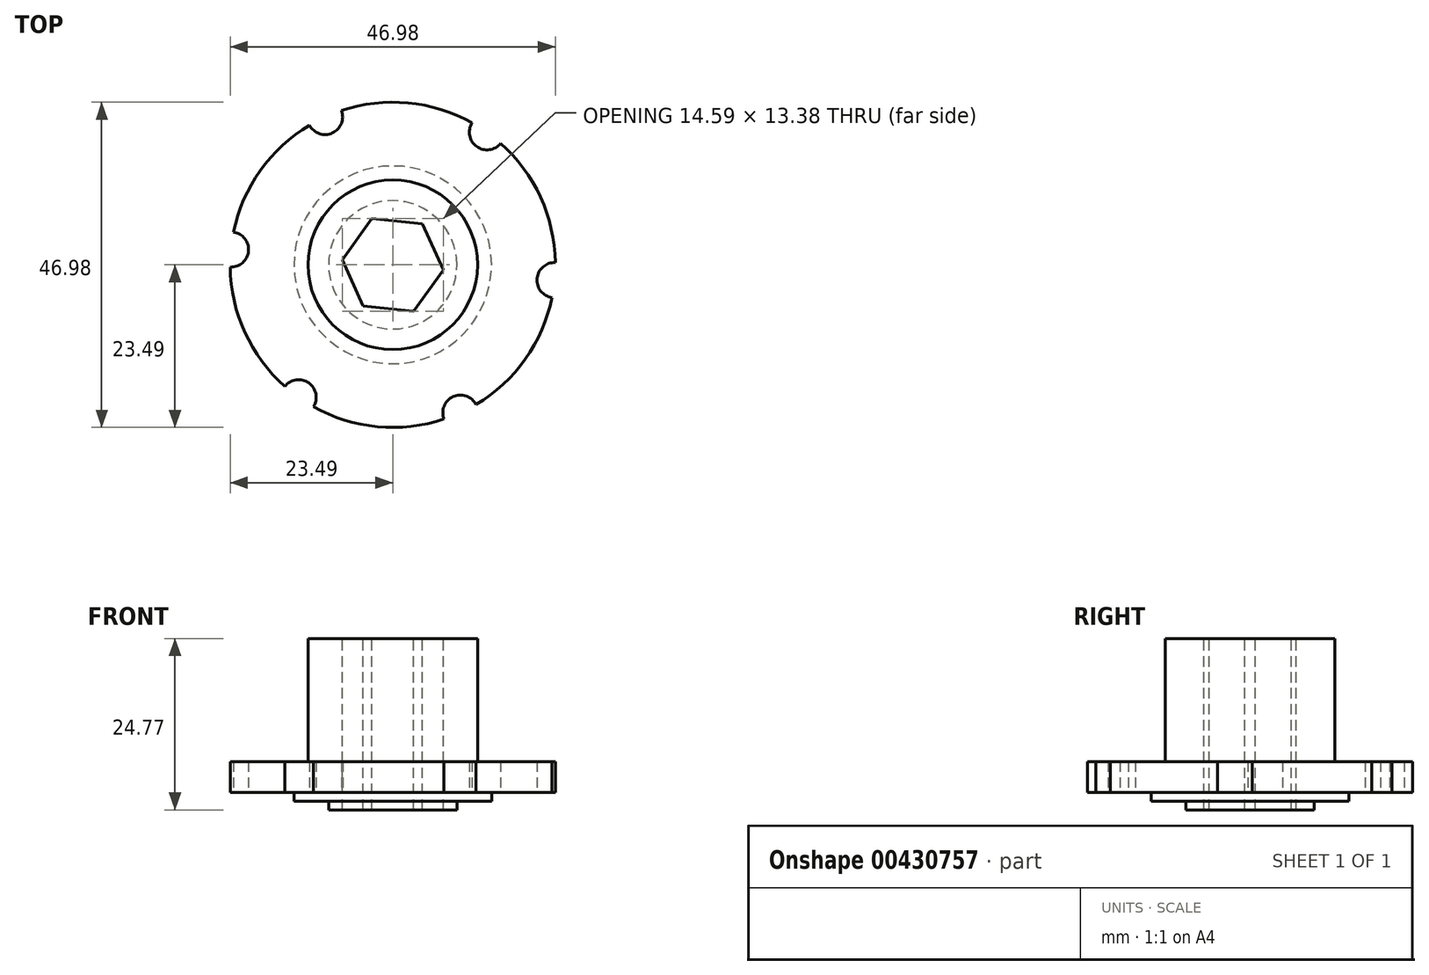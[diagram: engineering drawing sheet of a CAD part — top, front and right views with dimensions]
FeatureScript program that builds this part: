
annotation { "Feature Type Name" : "Feature", "Feature Type Description" : "" }
export const myFeature = defineFeature(function(context is Context, id is Id, definition is map)
    precondition{}
    {
        {
            var Q0;
            Q0=qCreatedBy(makeId("Top.planeOp"),FACE);
            var sketch = newSketch(context, id + "F0", { "sketchPlane" : qUnion([Q0])});
            skCircle(sketch, "E0", {"center": v(0, 0) * mm, "radius": 27.3 * mm});
            skCircle(sketch, "E1", {"center": v(0, 0) * mm, "radius": 23.5 * mm});
            skCircle(sketch, "E2", {"center": v(0, 0) * mm, "radius": 14.29 * mm});
            skCircle(sketch, "E3", {"center": v(0, 0) * mm, "radius": 9.27 * mm});
            skCircle(sketch, "E4.cCircle", {"center": v(0, 0) * mm, "radius": 23.5 * mm, "construction": true});
            skLineSegment(sketch, "E4.0", {"start": v(-9.78, 21.36) * mm, "end": v(13.6, 19.15) * mm});
            skLineSegment(sketch, "E4.1", {"start": v(13.6, 19.15) * mm, "end": v(23.4, -2.2) * mm});
            skLineSegment(sketch, "E4.2", {"start": v(23.4, -2.2) * mm, "end": v(9.78, -21.36) * mm});
            skLineSegment(sketch, "E4.3", {"start": v(9.78, -21.36) * mm, "end": v(-13.6, -19.15) * mm});
            skLineSegment(sketch, "E4.4", {"start": v(-13.6, -19.15) * mm, "end": v(-23.4, 2.2) * mm});
            skLineSegment(sketch, "E4.5", {"start": v(-23.4, 2.2) * mm, "end": v(-9.78, 21.36) * mm});
            skCircle(sketch, "E5", {"center": v(9.78, -21.36) * mm, "radius": 2.54 * mm});
            skCircle(sketch, "E6", {"center": v(-13.6, -19.15) * mm, "radius": 2.54 * mm});
            skCircle(sketch, "E7", {"center": v(23.4, -2.2) * mm, "radius": 2.54 * mm});
            skCircle(sketch, "E8", {"center": v(13.6, 19.15) * mm, "radius": 2.54 * mm});
            skCircle(sketch, "E9", {"center": v(-9.78, 21.36) * mm, "radius": 2.54 * mm});
            skCircle(sketch, "E10", {"center": v(-23.4, 2.2) * mm, "radius": 2.54 * mm});
            skSolve(sketch);
        }
        {
            var Q0;
            Q0=makeQuery(id+"F0.imprint","IMPRINT",FACE,{"disambiguationData":[TD([[makeQuery(id+"F0.imprint","IMPRINT",EDGE,{"derivedFrom":sQuery(id+"F0.wireOp",EDGE,"E0")}),1.0]])]});
            var Q1;
            Q1=makeQuery(id+"F0.imprint","IMPRINT",FACE,{"disambiguationData":[TD([[makeQuery(id+"F0.imprint","IMPRINT",EDGE,{"derivedFrom":sQuery(id+"F0.wireOp",EDGE,"E1")}),1.0]])]});
            var Q2;
            Q2=makeQuery(id+"F0.imprint","IMPRINT",FACE,{"disambiguationData":[TD([[makeQuery(id+"F0.imprint","IMPRINT",EDGE,{"derivedFrom":sQuery(id+"F0.wireOp",EDGE,"E2")}),1.0]])]});
            var Q3;
            Q3=makeQuery(id+"F0.imprint","IMPRINT",FACE,{"disambiguationData":[TD([[makeQuery(id+"F0.imprint","IMPRINT",EDGE,{"derivedFrom":sQuery(id+"F0.wireOp",EDGE,"E3")}),1.0]])]});
            var Q4;
            Q4=makeQuery(id+"F0.imprint","IMPRINT",FACE,{"disambiguationData":[TD([[makeQuery(id+"F0.imprint","IMPRINT",EDGE,{"derivedFrom":sQuery(id+"F0.wireOp",EDGE,"E2")}),-1.0]])]});
            var Q5;
            {var subQ0=sQuery(id+"F0.wireOp",EDGE,"E9");var subQ1=sQuery(id+"F0.wireOp",EDGE,"E1");var subQ2=makeQuery(id+"F0.imprint","INTERSECT",VERTEX,{"disambiguationData":[OD(1.0)],"derivedFrom":[subQ1,subQ0]});Q5=makeQuery(id+"F0.imprint","IMPRINT",FACE,{"disambiguationData":[TD([[makeQuery(id+"F0.imprint","IMPRINT",EDGE,{"disambiguationData":[TD([[subQ2,-1.0]])],"derivedFrom":subQ1}),1.0]])]});}
            var Q6;
            {var subQ0=sQuery(id+"F0.wireOp",EDGE,"E10");var subQ1=sQuery(id+"F0.wireOp",EDGE,"E1");var subQ2=makeQuery(id+"F0.imprint","INTERSECT",VERTEX,{"disambiguationData":[OD(1.0)],"derivedFrom":[subQ1,subQ0]});Q6=makeQuery(id+"F0.imprint","IMPRINT",FACE,{"disambiguationData":[TD([[makeQuery(id+"F0.imprint","IMPRINT",EDGE,{"disambiguationData":[TD([[subQ2,-1.0]])],"derivedFrom":subQ1}),1.0]])]});}
            var Q7;
            {var subQ0=sQuery(id+"F0.wireOp",EDGE,"E6");var subQ1=sQuery(id+"F0.wireOp",EDGE,"E1");var subQ2=makeQuery(id+"F0.imprint","INTERSECT",VERTEX,{"disambiguationData":[OD(1.0)],"derivedFrom":[subQ1,subQ0]});Q7=makeQuery(id+"F0.imprint","IMPRINT",FACE,{"disambiguationData":[TD([[makeQuery(id+"F0.imprint","IMPRINT",EDGE,{"disambiguationData":[TD([[subQ2,-1.0]])],"derivedFrom":subQ1}),1.0]])]});}
            var Q8;
            {var subQ0=sQuery(id+"F0.wireOp",EDGE,"E5");var subQ1=sQuery(id+"F0.wireOp",EDGE,"E1");var subQ2=makeQuery(id+"F0.imprint","INTERSECT",VERTEX,{"disambiguationData":[OD(1.0)],"derivedFrom":[subQ1,subQ0]});Q8=makeQuery(id+"F0.imprint","IMPRINT",FACE,{"disambiguationData":[TD([[makeQuery(id+"F0.imprint","IMPRINT",EDGE,{"disambiguationData":[TD([[subQ2,-1.0]])],"derivedFrom":subQ1}),1.0]])]});}
            var Q9;
            {var subQ0=sQuery(id+"F0.wireOp",EDGE,"E8");var subQ1=sQuery(id+"F0.wireOp",EDGE,"E1");var subQ2=makeQuery(id+"F0.imprint","INTERSECT",VERTEX,{"disambiguationData":[OD(0.0)],"derivedFrom":[subQ1,subQ0]});Q9=makeQuery(id+"F0.imprint","IMPRINT",FACE,{"disambiguationData":[TD([[makeQuery(id+"F0.imprint","IMPRINT",EDGE,{"disambiguationData":[TD([[subQ2,1.0]])],"derivedFrom":subQ1}),1.0]])]});}
            var Q10;
            {var subQ0=sQuery(id+"F0.wireOp",EDGE,"E8");var subQ1=sQuery(id+"F0.wireOp",EDGE,"E1");var subQ2=makeQuery(id+"F0.imprint","INTERSECT",VERTEX,{"disambiguationData":[OD(1.0)],"derivedFrom":[subQ1,subQ0]});Q10=makeQuery(id+"F0.imprint","IMPRINT",FACE,{"disambiguationData":[TD([[makeQuery(id+"F0.imprint","IMPRINT",EDGE,{"disambiguationData":[TD([[subQ2,-1.0]])],"derivedFrom":subQ1}),1.0]])]});}
            var Q11;
            {var subQ0=sQuery(id+"F0.wireOp",EDGE,"E9");var subQ1=sQuery(id+"F0.wireOp",EDGE,"E0");var subQ2=makeQuery(id+"F0.imprint","INTERSECT",VERTEX,{"disambiguationData":[OD(0.0)],"derivedFrom":[subQ1,subQ0]});Q11=makeQuery(id+"F0.imprint","IMPRINT",FACE,{"disambiguationData":[TD([[makeQuery(id+"F0.imprint","IMPRINT",EDGE,{"disambiguationData":[TD([[subQ2,-1.0]])],"derivedFrom":subQ1}),-1.0]])]});}
            var Q12;
            {var subQ0=sQuery(id+"F0.wireOp",EDGE,"E9");var subQ1=sQuery(id+"F0.wireOp",EDGE,"E0");var subQ2=makeQuery(id+"F0.imprint","INTERSECT",VERTEX,{"disambiguationData":[OD(0.0)],"derivedFrom":[subQ1,subQ0]});Q12=makeQuery(id+"F0.imprint","IMPRINT",FACE,{"disambiguationData":[TD([[makeQuery(id+"F0.imprint","IMPRINT",EDGE,{"disambiguationData":[TD([[subQ2,-1.0]])],"derivedFrom":subQ1}),1.0]])]});}
            var Q13;
            {var subQ1=sQuery(id+"F0.wireOp",EDGE,"E4.0");var subQ3=sQuery(id+"F0.wireOp",EDGE,"E9");var subQ4=makeQuery(id+"F0.imprint","INTERSECT",VERTEX,{"derivedFrom":[subQ1,subQ3]});Q13=makeQuery(id+"F0.imprint","IMPRINT",FACE,{"disambiguationData":[TD([[makeQuery(id+"F0.imprint","IMPRINT",EDGE,{"disambiguationData":[TD([[subQ4,1.0]])],"derivedFrom":subQ3}),1.0]])]});}
            var Q14;
            {var subQ1=sQuery(id+"F0.wireOp",EDGE,"E4.4");var subQ3=sQuery(id+"F0.wireOp",EDGE,"E10");var subQ4=makeQuery(id+"F0.imprint","INTERSECT",VERTEX,{"derivedFrom":[subQ1,subQ3]});Q14=makeQuery(id+"F0.imprint","IMPRINT",FACE,{"disambiguationData":[TD([[makeQuery(id+"F0.imprint","IMPRINT",EDGE,{"disambiguationData":[TD([[subQ4,-1.0]])],"derivedFrom":subQ3}),1.0]])]});}
            var Q15;
            {var subQ0=sQuery(id+"F0.wireOp",EDGE,"E10");var subQ1=sQuery(id+"F0.wireOp",EDGE,"E0");var subQ2=makeQuery(id+"F0.imprint","INTERSECT",VERTEX,{"disambiguationData":[OD(0.0)],"derivedFrom":[subQ1,subQ0]});Q15=makeQuery(id+"F0.imprint","IMPRINT",FACE,{"disambiguationData":[TD([[makeQuery(id+"F0.imprint","IMPRINT",EDGE,{"disambiguationData":[TD([[subQ2,-1.0]])],"derivedFrom":subQ1}),1.0]])]});}
            var Q16;
            {var subQ0=sQuery(id+"F0.wireOp",EDGE,"E10");var subQ1=sQuery(id+"F0.wireOp",EDGE,"E0");var subQ2=makeQuery(id+"F0.imprint","INTERSECT",VERTEX,{"disambiguationData":[OD(0.0)],"derivedFrom":[subQ1,subQ0]});Q16=makeQuery(id+"F0.imprint","IMPRINT",FACE,{"disambiguationData":[TD([[makeQuery(id+"F0.imprint","IMPRINT",EDGE,{"disambiguationData":[TD([[subQ2,-1.0]])],"derivedFrom":subQ1}),-1.0]])]});}
            var Q17;
            {var subQ1=sQuery(id+"F0.wireOp",EDGE,"E4.3");var subQ3=sQuery(id+"F0.wireOp",EDGE,"E6");var subQ4=makeQuery(id+"F0.imprint","INTERSECT",VERTEX,{"derivedFrom":[subQ1,subQ3]});Q17=makeQuery(id+"F0.imprint","IMPRINT",FACE,{"disambiguationData":[TD([[makeQuery(id+"F0.imprint","IMPRINT",EDGE,{"disambiguationData":[TD([[subQ4,-1.0]])],"derivedFrom":subQ3}),1.0]])]});}
            var Q18;
            {var subQ2=sQuery(id+"F0.wireOp",EDGE,"E6");var subQ4=sQuery(id+"F0.wireOp",EDGE,"E0");var subQ5=makeQuery(id+"F0.imprint","INTERSECT",VERTEX,{"disambiguationData":[OD(0.0)],"derivedFrom":[subQ4,subQ2]});Q18=makeQuery(id+"F0.imprint","IMPRINT",FACE,{"disambiguationData":[TD([[makeQuery(id+"F0.imprint","IMPRINT",EDGE,{"disambiguationData":[TD([[subQ5,-1.0]])],"derivedFrom":subQ4}),1.0]])]});}
            var Q19;
            {var subQ0=sQuery(id+"F0.wireOp",EDGE,"E6");var subQ1=sQuery(id+"F0.wireOp",EDGE,"E0");var subQ2=makeQuery(id+"F0.imprint","INTERSECT",VERTEX,{"disambiguationData":[OD(0.0)],"derivedFrom":[subQ1,subQ0]});Q19=makeQuery(id+"F0.imprint","IMPRINT",FACE,{"disambiguationData":[TD([[makeQuery(id+"F0.imprint","IMPRINT",EDGE,{"disambiguationData":[TD([[subQ2,-1.0]])],"derivedFrom":subQ1}),-1.0]])]});}
            var Q20;
            {var subQ1=sQuery(id+"F0.wireOp",EDGE,"E4.2");var subQ3=sQuery(id+"F0.wireOp",EDGE,"E5");var subQ4=makeQuery(id+"F0.imprint","INTERSECT",VERTEX,{"derivedFrom":[subQ1,subQ3]});Q20=makeQuery(id+"F0.imprint","IMPRINT",FACE,{"disambiguationData":[TD([[makeQuery(id+"F0.imprint","IMPRINT",EDGE,{"disambiguationData":[TD([[subQ4,-1.0]])],"derivedFrom":subQ3}),1.0]])]});}
            var Q21;
            {var subQ2=sQuery(id+"F0.wireOp",EDGE,"E5");var subQ5=sQuery(id+"F0.wireOp",EDGE,"E0");var subQ6=makeQuery(id+"F0.imprint","INTERSECT",VERTEX,{"disambiguationData":[OD(0.0)],"derivedFrom":[subQ5,subQ2]});Q21=makeQuery(id+"F0.imprint","IMPRINT",FACE,{"disambiguationData":[TD([[makeQuery(id+"F0.imprint","IMPRINT",EDGE,{"disambiguationData":[TD([[subQ6,-1.0]])],"derivedFrom":subQ5}),1.0]])]});}
            var Q22;
            {var subQ0=sQuery(id+"F0.wireOp",EDGE,"E5");var subQ1=sQuery(id+"F0.wireOp",EDGE,"E0");var subQ2=makeQuery(id+"F0.imprint","INTERSECT",VERTEX,{"disambiguationData":[OD(0.0)],"derivedFrom":[subQ1,subQ0]});Q22=makeQuery(id+"F0.imprint","IMPRINT",FACE,{"disambiguationData":[TD([[makeQuery(id+"F0.imprint","IMPRINT",EDGE,{"disambiguationData":[TD([[subQ2,-1.0]])],"derivedFrom":subQ1}),-1.0]])]});}
            var Q23;
            {var subQ0=sQuery(id+"F0.wireOp",EDGE,"E7");var subQ1=sQuery(id+"F0.wireOp",EDGE,"E0");var subQ7=makeQuery(id+"F0.imprint","INTERSECT",VERTEX,{"disambiguationData":[OD(0.0)],"derivedFrom":[subQ1,subQ0]});Q23=makeQuery(id+"F0.imprint","IMPRINT",FACE,{"disambiguationData":[TD([[makeQuery(id+"F0.imprint","IMPRINT",EDGE,{"disambiguationData":[TD([[subQ7,-1.0]])],"derivedFrom":subQ1}),1.0]])]});}
            var Q24;
            {var subQ0=sQuery(id+"F0.wireOp",EDGE,"E7");var subQ1=sQuery(id+"F0.wireOp",EDGE,"E0");var subQ2=makeQuery(id+"F0.imprint","INTERSECT",VERTEX,{"disambiguationData":[OD(0.0)],"derivedFrom":[subQ1,subQ0]});Q24=makeQuery(id+"F0.imprint","IMPRINT",FACE,{"disambiguationData":[TD([[makeQuery(id+"F0.imprint","IMPRINT",EDGE,{"disambiguationData":[TD([[subQ2,-1.0]])],"derivedFrom":subQ1}),-1.0]])]});}
            var Q25;
            {var subQ1=sQuery(id+"F0.wireOp",EDGE,"E4.1");var subQ3=sQuery(id+"F0.wireOp",EDGE,"E7");var subQ4=makeQuery(id+"F0.imprint","INTERSECT",VERTEX,{"derivedFrom":[subQ1,subQ3]});Q25=makeQuery(id+"F0.imprint","IMPRINT",FACE,{"disambiguationData":[TD([[makeQuery(id+"F0.imprint","IMPRINT",EDGE,{"disambiguationData":[TD([[subQ4,-1.0]])],"derivedFrom":subQ3}),1.0]])]});}
            var Q26;
            {var subQ1=sQuery(id+"F0.wireOp",EDGE,"E4.0");var subQ3=sQuery(id+"F0.wireOp",EDGE,"E8");var subQ4=makeQuery(id+"F0.imprint","INTERSECT",VERTEX,{"derivedFrom":[subQ1,subQ3]});Q26=makeQuery(id+"F0.imprint","IMPRINT",FACE,{"disambiguationData":[TD([[makeQuery(id+"F0.imprint","IMPRINT",EDGE,{"disambiguationData":[TD([[subQ4,-1.0]])],"derivedFrom":subQ3}),1.0]])]});}
            var Q27;
            {var subQ0=sQuery(id+"F0.wireOp",EDGE,"E8");var subQ1=sQuery(id+"F0.wireOp",EDGE,"E0");var subQ2=makeQuery(id+"F0.imprint","INTERSECT",VERTEX,{"disambiguationData":[OD(0.0)],"derivedFrom":[subQ1,subQ0]});Q27=makeQuery(id+"F0.imprint","IMPRINT",FACE,{"disambiguationData":[TD([[makeQuery(id+"F0.imprint","IMPRINT",EDGE,{"disambiguationData":[TD([[subQ2,1.0]])],"derivedFrom":subQ1}),1.0]])]});}
            var Q28;
            {var subQ0=sQuery(id+"F0.wireOp",EDGE,"E8");var subQ1=sQuery(id+"F0.wireOp",EDGE,"E0");var subQ2=makeQuery(id+"F0.imprint","INTERSECT",VERTEX,{"disambiguationData":[OD(0.0)],"derivedFrom":[subQ1,subQ0]});Q28=makeQuery(id+"F0.imprint","IMPRINT",FACE,{"disambiguationData":[TD([[makeQuery(id+"F0.imprint","IMPRINT",EDGE,{"disambiguationData":[TD([[subQ2,1.0]])],"derivedFrom":subQ1}),-1.0]])]});}
            extrude(context, id + "F1", {"entities" : qUnion([Q0, Q1, Q2, Q3, Q4, Q5, Q6, Q7, Q8, Q9, Q10, Q11, Q12, Q13, Q14, Q15, Q16, Q17, Q18, Q19, Q20, Q21, Q22, Q23, Q24, Q25, Q26, Q27, Q28]), "depth" : 4.44 * mm, "offsetDistance" : 25.4 * mm});
        }
        {
            var Q0;
            Q0=makeQuery(id+"F1.opExtrude","CAP_FACE",FACE,{"disambiguationData":[OSD([sQuery(id+"F0.wireOp",EDGE,"E0")])],"isStart":false});
            var sketch = newSketch(context, id + "F2", { "sketchPlane" : qUnion([Q0])});
            skCircle(sketch, "E11", {"center": v(0, 0) * mm, "radius": 12.26 * mm});
            skCircle(sketch, "E12", {"center": v(0, 0) * mm, "radius": 14.29 * mm});
            skSolve(sketch);
        }
        {
            var Q0;
            Q0=makeQuery(id+"F2.imprint","IMPRINT",FACE,{"disambiguationData":[TD([[makeQuery(id+"F2.imprint","IMPRINT",EDGE,{"derivedFrom":sQuery(id+"F2.wireOp",EDGE,"E11")}),1.0]])]});
            extrude(context, id + "F3", {"entities" : qUnion([Q0]), "operationType" : NewBodyOperationType.ADD, "depth" : 17.78 * mm, "offsetDistance" : 25.4 * mm});
        }
        {
            var Q0;
            Q0=makeQuery(id+"F0.imprint","IMPRINT",FACE,{"disambiguationData":[TD([[makeQuery(id+"F0.imprint","IMPRINT",EDGE,{"derivedFrom":sQuery(id+"F0.wireOp",EDGE,"E3")}),1.0]])]});
            extrude(context, id + "F4", {"entities" : qUnion([Q0]), "operationType" : NewBodyOperationType.ADD, "oppositeDirection" : true, "depth" : 2.54 * mm, "offsetDistance" : 25.4 * mm});
        }
        {
            var Q0;
            Q0=makeQuery(id+"F0.imprint","IMPRINT",FACE,{"disambiguationData":[TD([[makeQuery(id+"F0.imprint","IMPRINT",EDGE,{"derivedFrom":sQuery(id+"F0.wireOp",EDGE,"E2")}),1.0]])]});
            extrude(context, id + "F5", {"entities" : qUnion([Q0]), "operationType" : NewBodyOperationType.ADD, "oppositeDirection" : true, "depth" : 1.27 * mm, "offsetDistance" : 25.4 * mm});
        }
        {
            var Q0;
            Q0=makeQuery(id+"F3.opExtrude","CAP_FACE",FACE,{"disambiguationData":[OSD([sQuery(id+"F2.wireOp",EDGE,"E11")])],"isStart":false});
            var sketch = newSketch(context, id + "F6", { "sketchPlane" : qUnion([Q0])});
            skCircle(sketch, "E13.cCircle", {"center": v(0, 0) * mm, "radius": 7.33 * mm, "construction": true});
            skLineSegment(sketch, "E13.0", {"start": v(3, -6.69) * mm, "end": v(-4.29, -5.95) * mm});
            skLineSegment(sketch, "E13.1", {"start": v(-4.29, -5.95) * mm, "end": v(-7.3, 0.74) * mm});
            skLineSegment(sketch, "E13.2", {"start": v(-7.3, 0.74) * mm, "end": v(-3, 6.69) * mm});
            skLineSegment(sketch, "E13.3", {"start": v(-3, 6.69) * mm, "end": v(4.29, 5.95) * mm});
            skLineSegment(sketch, "E13.4", {"start": v(4.29, 5.95) * mm, "end": v(7.3, -0.74) * mm});
            skLineSegment(sketch, "E13.5", {"start": v(7.3, -0.74) * mm, "end": v(3, -6.69) * mm});
            skSolve(sketch);
        }
        {
            var Q0;
            Q0=makeQuery(id+"F6.imprint","IMPRINT",FACE,{"disambiguationData":[TD([[makeQuery(id+"F6.imprint","IMPRINT",EDGE,{"derivedFrom":sQuery(id+"F6.wireOp",EDGE,"E13.0")}),-1.0]])]});
            extrude(context, id + "F7", {"entities" : qUnion([Q0]), "operationType" : NewBodyOperationType.REMOVE, "oppositeDirection" : true, "depth" : 25.4 * mm, "offsetDistance" : 25.4 * mm});
        }
        {
            var Q0;
            {var subQ1=sQuery(id+"F0.wireOp",EDGE,"E4.0");var subQ3=sQuery(id+"F0.wireOp",EDGE,"E8");var subQ4=makeQuery(id+"F0.imprint","INTERSECT",VERTEX,{"derivedFrom":[subQ1,subQ3]});Q0=makeQuery(id+"F0.imprint","IMPRINT",FACE,{"disambiguationData":[TD([[makeQuery(id+"F0.imprint","IMPRINT",EDGE,{"disambiguationData":[TD([[subQ4,-1.0]])],"derivedFrom":subQ3}),1.0]])]});}
            var Q1;
            {var subQ1=sQuery(id+"F0.wireOp",EDGE,"E1");var subQ3=sQuery(id+"F0.wireOp",EDGE,"E8");var subQ4=makeQuery(id+"F0.imprint","INTERSECT",VERTEX,{"disambiguationData":[OD(0.0)],"derivedFrom":[subQ1,subQ3]});Q1=makeQuery(id+"F0.imprint","IMPRINT",FACE,{"disambiguationData":[TD([[makeQuery(id+"F0.imprint","IMPRINT",EDGE,{"disambiguationData":[TD([[subQ4,1.0]])],"derivedFrom":subQ3}),1.0]])]});}
            var Q2;
            {var subQ1=sQuery(id+"F0.wireOp",EDGE,"E1");var subQ3=sQuery(id+"F0.wireOp",EDGE,"E8");var subQ4=makeQuery(id+"F0.imprint","INTERSECT",VERTEX,{"disambiguationData":[OD(1.0)],"derivedFrom":[subQ1,subQ3]});Q2=makeQuery(id+"F0.imprint","IMPRINT",FACE,{"disambiguationData":[TD([[makeQuery(id+"F0.imprint","IMPRINT",EDGE,{"disambiguationData":[TD([[subQ4,-1.0]])],"derivedFrom":subQ3}),1.0]])]});}
            var Q3;
            {var subQ0=sQuery(id+"F0.wireOp",EDGE,"E8");var subQ1=sQuery(id+"F0.wireOp",EDGE,"E0");var subQ2=makeQuery(id+"F0.imprint","INTERSECT",VERTEX,{"disambiguationData":[OD(0.0)],"derivedFrom":[subQ1,subQ0]});Q3=makeQuery(id+"F0.imprint","IMPRINT",FACE,{"disambiguationData":[TD([[makeQuery(id+"F0.imprint","IMPRINT",EDGE,{"disambiguationData":[TD([[subQ2,1.0]])],"derivedFrom":subQ1}),1.0]])]});}
            var Q4;
            {var subQ0=sQuery(id+"F0.wireOp",EDGE,"E8");var subQ1=sQuery(id+"F0.wireOp",EDGE,"E0");var subQ2=makeQuery(id+"F0.imprint","INTERSECT",VERTEX,{"disambiguationData":[OD(0.0)],"derivedFrom":[subQ1,subQ0]});Q4=makeQuery(id+"F0.imprint","IMPRINT",FACE,{"disambiguationData":[TD([[makeQuery(id+"F0.imprint","IMPRINT",EDGE,{"disambiguationData":[TD([[subQ2,1.0]])],"derivedFrom":subQ1}),-1.0]])]});}
            var Q5;
            {var subQ0=sQuery(id+"F0.wireOp",EDGE,"E10");var subQ1=sQuery(id+"F0.wireOp",EDGE,"E0");var subQ2=makeQuery(id+"F0.imprint","INTERSECT",VERTEX,{"disambiguationData":[OD(0.0)],"derivedFrom":[subQ1,subQ0]});Q5=makeQuery(id+"F0.imprint","IMPRINT",FACE,{"disambiguationData":[TD([[makeQuery(id+"F0.imprint","IMPRINT",EDGE,{"disambiguationData":[TD([[subQ2,-1.0]])],"derivedFrom":subQ1}),-1.0]])]});}
            var Q6;
            {var subQ0=sQuery(id+"F0.wireOp",EDGE,"E10");var subQ1=sQuery(id+"F0.wireOp",EDGE,"E0");var subQ2=makeQuery(id+"F0.imprint","INTERSECT",VERTEX,{"disambiguationData":[OD(0.0)],"derivedFrom":[subQ1,subQ0]});Q6=makeQuery(id+"F0.imprint","IMPRINT",FACE,{"disambiguationData":[TD([[makeQuery(id+"F0.imprint","IMPRINT",EDGE,{"disambiguationData":[TD([[subQ2,-1.0]])],"derivedFrom":subQ1}),1.0]])]});}
            var Q7;
            {var subQ1=sQuery(id+"F0.wireOp",EDGE,"E1");var subQ3=sQuery(id+"F0.wireOp",EDGE,"E10");var subQ4=makeQuery(id+"F0.imprint","INTERSECT",VERTEX,{"disambiguationData":[OD(0.0)],"derivedFrom":[subQ1,subQ3]});Q7=makeQuery(id+"F0.imprint","IMPRINT",FACE,{"disambiguationData":[TD([[makeQuery(id+"F0.imprint","IMPRINT",EDGE,{"disambiguationData":[TD([[subQ4,1.0]])],"derivedFrom":subQ3}),1.0]])]});}
            var Q8;
            {var subQ1=sQuery(id+"F0.wireOp",EDGE,"E4.4");var subQ3=sQuery(id+"F0.wireOp",EDGE,"E10");var subQ4=makeQuery(id+"F0.imprint","INTERSECT",VERTEX,{"derivedFrom":[subQ1,subQ3]});Q8=makeQuery(id+"F0.imprint","IMPRINT",FACE,{"disambiguationData":[TD([[makeQuery(id+"F0.imprint","IMPRINT",EDGE,{"disambiguationData":[TD([[subQ4,-1.0]])],"derivedFrom":subQ3}),1.0]])]});}
            var Q9;
            {var subQ1=sQuery(id+"F0.wireOp",EDGE,"E1");var subQ3=sQuery(id+"F0.wireOp",EDGE,"E10");var subQ4=makeQuery(id+"F0.imprint","INTERSECT",VERTEX,{"disambiguationData":[OD(1.0)],"derivedFrom":[subQ1,subQ3]});Q9=makeQuery(id+"F0.imprint","IMPRINT",FACE,{"disambiguationData":[TD([[makeQuery(id+"F0.imprint","IMPRINT",EDGE,{"disambiguationData":[TD([[subQ4,-1.0]])],"derivedFrom":subQ3}),1.0]])]});}
            var Q10;
            {var subQ0=sQuery(id+"F0.wireOp",EDGE,"E9");var subQ1=sQuery(id+"F0.wireOp",EDGE,"E0");var subQ2=makeQuery(id+"F0.imprint","INTERSECT",VERTEX,{"disambiguationData":[OD(0.0)],"derivedFrom":[subQ1,subQ0]});Q10=makeQuery(id+"F0.imprint","IMPRINT",FACE,{"disambiguationData":[TD([[makeQuery(id+"F0.imprint","IMPRINT",EDGE,{"disambiguationData":[TD([[subQ2,-1.0]])],"derivedFrom":subQ1}),-1.0]])]});}
            var Q11;
            {var subQ0=sQuery(id+"F0.wireOp",EDGE,"E9");var subQ1=sQuery(id+"F0.wireOp",EDGE,"E0");var subQ2=makeQuery(id+"F0.imprint","INTERSECT",VERTEX,{"disambiguationData":[OD(0.0)],"derivedFrom":[subQ1,subQ0]});Q11=makeQuery(id+"F0.imprint","IMPRINT",FACE,{"disambiguationData":[TD([[makeQuery(id+"F0.imprint","IMPRINT",EDGE,{"disambiguationData":[TD([[subQ2,-1.0]])],"derivedFrom":subQ1}),1.0]])]});}
            var Q12;
            {var subQ1=sQuery(id+"F0.wireOp",EDGE,"E1");var subQ3=sQuery(id+"F0.wireOp",EDGE,"E9");var subQ4=makeQuery(id+"F0.imprint","INTERSECT",VERTEX,{"disambiguationData":[OD(1.0)],"derivedFrom":[subQ1,subQ3]});Q12=makeQuery(id+"F0.imprint","IMPRINT",FACE,{"disambiguationData":[TD([[makeQuery(id+"F0.imprint","IMPRINT",EDGE,{"disambiguationData":[TD([[subQ4,-1.0]])],"derivedFrom":subQ3}),1.0]])]});}
            var Q13;
            {var subQ1=sQuery(id+"F0.wireOp",EDGE,"E4.0");var subQ3=sQuery(id+"F0.wireOp",EDGE,"E9");var subQ4=makeQuery(id+"F0.imprint","INTERSECT",VERTEX,{"derivedFrom":[subQ1,subQ3]});Q13=makeQuery(id+"F0.imprint","IMPRINT",FACE,{"disambiguationData":[TD([[makeQuery(id+"F0.imprint","IMPRINT",EDGE,{"disambiguationData":[TD([[subQ4,1.0]])],"derivedFrom":subQ3}),1.0]])]});}
            var Q14;
            {var subQ1=sQuery(id+"F0.wireOp",EDGE,"E1");var subQ3=sQuery(id+"F0.wireOp",EDGE,"E9");var subQ4=makeQuery(id+"F0.imprint","INTERSECT",VERTEX,{"disambiguationData":[OD(0.0)],"derivedFrom":[subQ1,subQ3]});Q14=makeQuery(id+"F0.imprint","IMPRINT",FACE,{"disambiguationData":[TD([[makeQuery(id+"F0.imprint","IMPRINT",EDGE,{"disambiguationData":[TD([[subQ4,1.0]])],"derivedFrom":subQ3}),1.0]])]});}
            var Q15;
            {var subQ1=sQuery(id+"F0.wireOp",EDGE,"E4.3");var subQ3=sQuery(id+"F0.wireOp",EDGE,"E6");var subQ4=makeQuery(id+"F0.imprint","INTERSECT",VERTEX,{"derivedFrom":[subQ1,subQ3]});Q15=makeQuery(id+"F0.imprint","IMPRINT",FACE,{"disambiguationData":[TD([[makeQuery(id+"F0.imprint","IMPRINT",EDGE,{"disambiguationData":[TD([[subQ4,-1.0]])],"derivedFrom":subQ3}),1.0]])]});}
            var Q16;
            {var subQ2=sQuery(id+"F0.wireOp",EDGE,"E6");var subQ4=sQuery(id+"F0.wireOp",EDGE,"E0");var subQ5=makeQuery(id+"F0.imprint","INTERSECT",VERTEX,{"disambiguationData":[OD(0.0)],"derivedFrom":[subQ4,subQ2]});Q16=makeQuery(id+"F0.imprint","IMPRINT",FACE,{"disambiguationData":[TD([[makeQuery(id+"F0.imprint","IMPRINT",EDGE,{"disambiguationData":[TD([[subQ5,-1.0]])],"derivedFrom":subQ4}),1.0]])]});}
            var Q17;
            {var subQ1=sQuery(id+"F0.wireOp",EDGE,"E1");var subQ3=sQuery(id+"F0.wireOp",EDGE,"E6");var subQ4=makeQuery(id+"F0.imprint","INTERSECT",VERTEX,{"disambiguationData":[OD(1.0)],"derivedFrom":[subQ1,subQ3]});Q17=makeQuery(id+"F0.imprint","IMPRINT",FACE,{"disambiguationData":[TD([[makeQuery(id+"F0.imprint","IMPRINT",EDGE,{"disambiguationData":[TD([[subQ4,-1.0]])],"derivedFrom":subQ3}),1.0]])]});}
            var Q18;
            {var subQ1=sQuery(id+"F0.wireOp",EDGE,"E1");var subQ3=sQuery(id+"F0.wireOp",EDGE,"E6");var subQ4=makeQuery(id+"F0.imprint","INTERSECT",VERTEX,{"disambiguationData":[OD(0.0)],"derivedFrom":[subQ1,subQ3]});Q18=makeQuery(id+"F0.imprint","IMPRINT",FACE,{"disambiguationData":[TD([[makeQuery(id+"F0.imprint","IMPRINT",EDGE,{"disambiguationData":[TD([[subQ4,1.0]])],"derivedFrom":subQ3}),1.0]])]});}
            var Q19;
            {var subQ0=sQuery(id+"F0.wireOp",EDGE,"E6");var subQ1=sQuery(id+"F0.wireOp",EDGE,"E0");var subQ2=makeQuery(id+"F0.imprint","INTERSECT",VERTEX,{"disambiguationData":[OD(0.0)],"derivedFrom":[subQ1,subQ0]});Q19=makeQuery(id+"F0.imprint","IMPRINT",FACE,{"disambiguationData":[TD([[makeQuery(id+"F0.imprint","IMPRINT",EDGE,{"disambiguationData":[TD([[subQ2,-1.0]])],"derivedFrom":subQ1}),-1.0]])]});}
            var Q20;
            {var subQ1=sQuery(id+"F0.wireOp",EDGE,"E4.2");var subQ3=sQuery(id+"F0.wireOp",EDGE,"E5");var subQ4=makeQuery(id+"F0.imprint","INTERSECT",VERTEX,{"derivedFrom":[subQ1,subQ3]});Q20=makeQuery(id+"F0.imprint","IMPRINT",FACE,{"disambiguationData":[TD([[makeQuery(id+"F0.imprint","IMPRINT",EDGE,{"disambiguationData":[TD([[subQ4,-1.0]])],"derivedFrom":subQ3}),1.0]])]});}
            var Q21;
            {var subQ2=sQuery(id+"F0.wireOp",EDGE,"E5");var subQ5=sQuery(id+"F0.wireOp",EDGE,"E0");var subQ6=makeQuery(id+"F0.imprint","INTERSECT",VERTEX,{"disambiguationData":[OD(0.0)],"derivedFrom":[subQ5,subQ2]});Q21=makeQuery(id+"F0.imprint","IMPRINT",FACE,{"disambiguationData":[TD([[makeQuery(id+"F0.imprint","IMPRINT",EDGE,{"disambiguationData":[TD([[subQ6,-1.0]])],"derivedFrom":subQ5}),1.0]])]});}
            var Q22;
            {var subQ0=sQuery(id+"F0.wireOp",EDGE,"E5");var subQ1=sQuery(id+"F0.wireOp",EDGE,"E0");var subQ2=makeQuery(id+"F0.imprint","INTERSECT",VERTEX,{"disambiguationData":[OD(0.0)],"derivedFrom":[subQ1,subQ0]});Q22=makeQuery(id+"F0.imprint","IMPRINT",FACE,{"disambiguationData":[TD([[makeQuery(id+"F0.imprint","IMPRINT",EDGE,{"disambiguationData":[TD([[subQ2,-1.0]])],"derivedFrom":subQ1}),-1.0]])]});}
            var Q23;
            {var subQ1=sQuery(id+"F0.wireOp",EDGE,"E1");var subQ3=sQuery(id+"F0.wireOp",EDGE,"E5");var subQ4=makeQuery(id+"F0.imprint","INTERSECT",VERTEX,{"disambiguationData":[OD(0.0)],"derivedFrom":[subQ1,subQ3]});Q23=makeQuery(id+"F0.imprint","IMPRINT",FACE,{"disambiguationData":[TD([[makeQuery(id+"F0.imprint","IMPRINT",EDGE,{"disambiguationData":[TD([[subQ4,1.0]])],"derivedFrom":subQ3}),1.0]])]});}
            var Q24;
            {var subQ1=sQuery(id+"F0.wireOp",EDGE,"E1");var subQ3=sQuery(id+"F0.wireOp",EDGE,"E5");var subQ4=makeQuery(id+"F0.imprint","INTERSECT",VERTEX,{"disambiguationData":[OD(1.0)],"derivedFrom":[subQ1,subQ3]});Q24=makeQuery(id+"F0.imprint","IMPRINT",FACE,{"disambiguationData":[TD([[makeQuery(id+"F0.imprint","IMPRINT",EDGE,{"disambiguationData":[TD([[subQ4,-1.0]])],"derivedFrom":subQ3}),1.0]])]});}
            var Q25;
            {var subQ0=sQuery(id+"F0.wireOp",EDGE,"E7");var subQ1=sQuery(id+"F0.wireOp",EDGE,"E0");var subQ7=makeQuery(id+"F0.imprint","INTERSECT",VERTEX,{"disambiguationData":[OD(0.0)],"derivedFrom":[subQ1,subQ0]});Q25=makeQuery(id+"F0.imprint","IMPRINT",FACE,{"disambiguationData":[TD([[makeQuery(id+"F0.imprint","IMPRINT",EDGE,{"disambiguationData":[TD([[subQ7,-1.0]])],"derivedFrom":subQ1}),1.0]])]});}
            var Q26;
            {var subQ1=sQuery(id+"F0.wireOp",EDGE,"E4.1");var subQ3=sQuery(id+"F0.wireOp",EDGE,"E7");var subQ4=makeQuery(id+"F0.imprint","INTERSECT",VERTEX,{"derivedFrom":[subQ1,subQ3]});Q26=makeQuery(id+"F0.imprint","IMPRINT",FACE,{"disambiguationData":[TD([[makeQuery(id+"F0.imprint","IMPRINT",EDGE,{"disambiguationData":[TD([[subQ4,-1.0]])],"derivedFrom":subQ3}),1.0]])]});}
            var Q27;
            {var subQ1=sQuery(id+"F0.wireOp",EDGE,"E1");var subQ3=sQuery(id+"F0.wireOp",EDGE,"E7");var subQ4=makeQuery(id+"F0.imprint","INTERSECT",VERTEX,{"disambiguationData":[OD(0.0)],"derivedFrom":[subQ1,subQ3]});Q27=makeQuery(id+"F0.imprint","IMPRINT",FACE,{"disambiguationData":[TD([[makeQuery(id+"F0.imprint","IMPRINT",EDGE,{"disambiguationData":[TD([[subQ4,-1.0]])],"derivedFrom":subQ3}),1.0]])]});}
            var Q28;
            {var subQ1=sQuery(id+"F0.wireOp",EDGE,"E1");var subQ3=sQuery(id+"F0.wireOp",EDGE,"E7");var subQ4=makeQuery(id+"F0.imprint","INTERSECT",VERTEX,{"disambiguationData":[OD(1.0)],"derivedFrom":[subQ1,subQ3]});Q28=makeQuery(id+"F0.imprint","IMPRINT",FACE,{"disambiguationData":[TD([[makeQuery(id+"F0.imprint","IMPRINT",EDGE,{"disambiguationData":[TD([[subQ4,1.0]])],"derivedFrom":subQ3}),1.0]])]});}
            var Q29;
            {var subQ0=sQuery(id+"F0.wireOp",EDGE,"E7");var subQ1=sQuery(id+"F0.wireOp",EDGE,"E0");var subQ2=makeQuery(id+"F0.imprint","INTERSECT",VERTEX,{"disambiguationData":[OD(0.0)],"derivedFrom":[subQ1,subQ0]});Q29=makeQuery(id+"F0.imprint","IMPRINT",FACE,{"disambiguationData":[TD([[makeQuery(id+"F0.imprint","IMPRINT",EDGE,{"disambiguationData":[TD([[subQ2,-1.0]])],"derivedFrom":subQ1}),-1.0]])]});}
            extrude(context, id + "F8", {"entities" : qUnion([Q0, Q1, Q2, Q3, Q4, Q5, Q6, Q7, Q8, Q9, Q10, Q11, Q12, Q13, Q14, Q15, Q16, Q17, Q18, Q19, Q20, Q21, Q22, Q23, Q24, Q25, Q26, Q27, Q28, Q29]), "operationType" : NewBodyOperationType.REMOVE, "depth" : 25.4 * mm, "offsetDistance" : 25.4 * mm});
        }
    });
